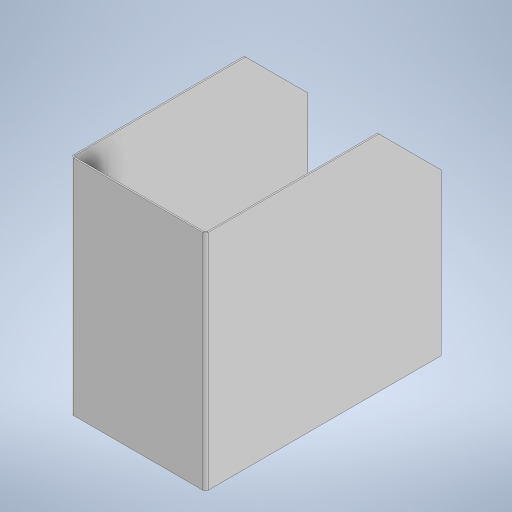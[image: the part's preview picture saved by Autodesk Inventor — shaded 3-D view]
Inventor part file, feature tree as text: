
AUTODESK INVENTOR PART (.ipt)
format: ipt  version: 2024.3 (Build 283343000, 343)  size: 361,984 bytes
history: native  units: mm
features: sheet_metal_op x9, sketch x6, other x6, projected_geometry x3, extrude x1
ambient origin geometry x8: Origin, YZ Plane, XZ Plane, XY Plane, X Axis, Y Axis, Z Axis, Center Point
bodies: Solid1 (feature_tree)
feature tree (25):
  sheet_metal_op  "Face1"
  sheet_metal_op  "Flange1"
  sheet_metal_op  "Flange2"
  sheet_metal_op  "Face2"
  extrude  "Extrusion1"  Depth=331.78mm
  sketch  "Sketch1"  dims[d0=350.0mm d1=331.78mm]
  other  "Plate1"
  sketch  "Sketch2"  dims[d2=239.261mm]
  other  "Plate2"
  sheet_metal_op  "Bend1"
  sheet_metal_op  "Corner1"
  sketch  "Sketch3"  dims[d3=45.0deg]
  other  "Plate3"
  sheet_metal_op  "Bend2"
  sheet_metal_op  "Corner2"
  sketch  "Sketch4"  dims[d4=2.0mm]
  sketch  "Sketch5"  dims[d5=2.0mm]
  projected_geometry  "Projected Loop1"
  projected_geometry  "Projected Loop2"
  other  "Plate4"
  sheet_metal_op  "Bend3"
  sketch  "Sketch6"  dims[d6=1.0mm d7=4.0mm d8=2.0mm d9=200.0mm d10=90.0deg d11=2.0mm d12=8.0mm d13=2.0mm d14=2.0mm d15=2.0mm d16=1.0mm d17=4.0mm d18=2.0mm d19=350.0mm d20=90.0deg d21=2.0mm d22=8.0mm d23=2.0mm d24=2.0mm d25=2.0mm d26=0.0mm d27=3.0mm d28=5.0mm d29=5.0mm d30=15.0mm d31=115.0mm d32=5.0mm d33=15.0mm d34=5.0mm d35=25.0mm d36=15.0mm d37=5.0mm d38=65.0mm d39=2.0mm d40=2.0mm d41=1.0mm d42=4.0mm d43=2.0mm d44=0.0mm d45=0.0mm]
  projected_geometry  "Projected Loop3"
  other  "Cut1"
  other  "Definition1"
